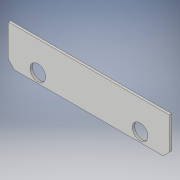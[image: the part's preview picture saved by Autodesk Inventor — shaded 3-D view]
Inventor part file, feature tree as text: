
AUTODESK INVENTOR PART (.ipt)
format: ipt  version: 2017 (Build 210142000, 142)  size: 133,120 bytes
history: native  units: in
note: dims shown in document units (in); Inventor stores cm internally (conversion verified against a paired STEP export)
features: extrude x3, sketch x3, thicken_offset x1
ambient origin geometry x8: Origin, YZ Plane, XZ Plane, XY Plane, X Axis, Y Axis, Z Axis, Center Point
bodies: Solid1 (feature_tree)
feature tree (7):
  extrude  "Extrusion1"  Depth=5.0in
  extrude  "Extrusion2"  Depth=0.25in TaperAngle=0.0deg
  sketch  "Sketch3"  dims[d10=1.7in d14=2.0in d15=0.0in d18=1.7in d19=1.5in d20=180.0deg d35=0.82in d36=0.82in d40=1.82in d41=0.146in d42=0.144in d43=0.146in d44=0.146in d45=3.175in d46=3.175in d47=2.899in d48=0.552in d49=0.1103in]
  extrude  "Extrusion3"  Depth=0.82in TaperAngle=0.0deg
  thicken_offset  "Thicken1"
  sketch  "Sketch1"  dims[d0=17.5in d1=5.0in]
  sketch  "Sketch2"  dims[d2=0.25in d3=0.0in d4=2.0in d5=0.0in]
